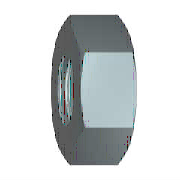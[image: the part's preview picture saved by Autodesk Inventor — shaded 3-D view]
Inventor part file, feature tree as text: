
AUTODESK INVENTOR PART (.ipt)
format: ipt  version: 2013 (Build 170138000, 138)  size: 169,472 bytes
history: native  units: mm (DEFAULTED — no unit token found)
features: sketch x3, chamfer x1, hole x1, other x1, plane x1
ambient origin geometry x7: Origin, YZ Plane, XZ Plane, X Axis, Y Axis, Z Axis, Center Point
bodies: Solid1 (feature_tree), Body (feature_tree)
feature tree (7):
  chamfer  "Chamfer1"  Distance=4.363323mm
  hole  "Thread"  [1 undecoded]
  other  "Work Axis1"
  plane  "Work Plane1"
  sketch  "Sketch1"  dims[d0=15.011107mm]
  sketch  "Sketch2"  dims[d1=6.8mm]
  sketch  "Sketch3"  dims[d2=0.0mm d3=4.363323mm d4=4.363323mm d5=13.0mm d6=13.0mm d7=90.0deg d25=1.221mm d26=6.0mm d27=4.0mm d28=2.0mm d29=14.3117mm d30=8.0mm d31=20.594885mm d8=0.676582mm d9=30.0deg d10=0.676582mm d11=30.0deg d13=0.0mm d14=0.0mm d39=0.0mm d40=0.676582mm d41=0.676582mm d42=0.0mm]
note: 1 required parameter value undecoded (feature->parameter linkage not recoverable at this tier; creation-order binding heuristic only, values carry confidence <= 0.55)
